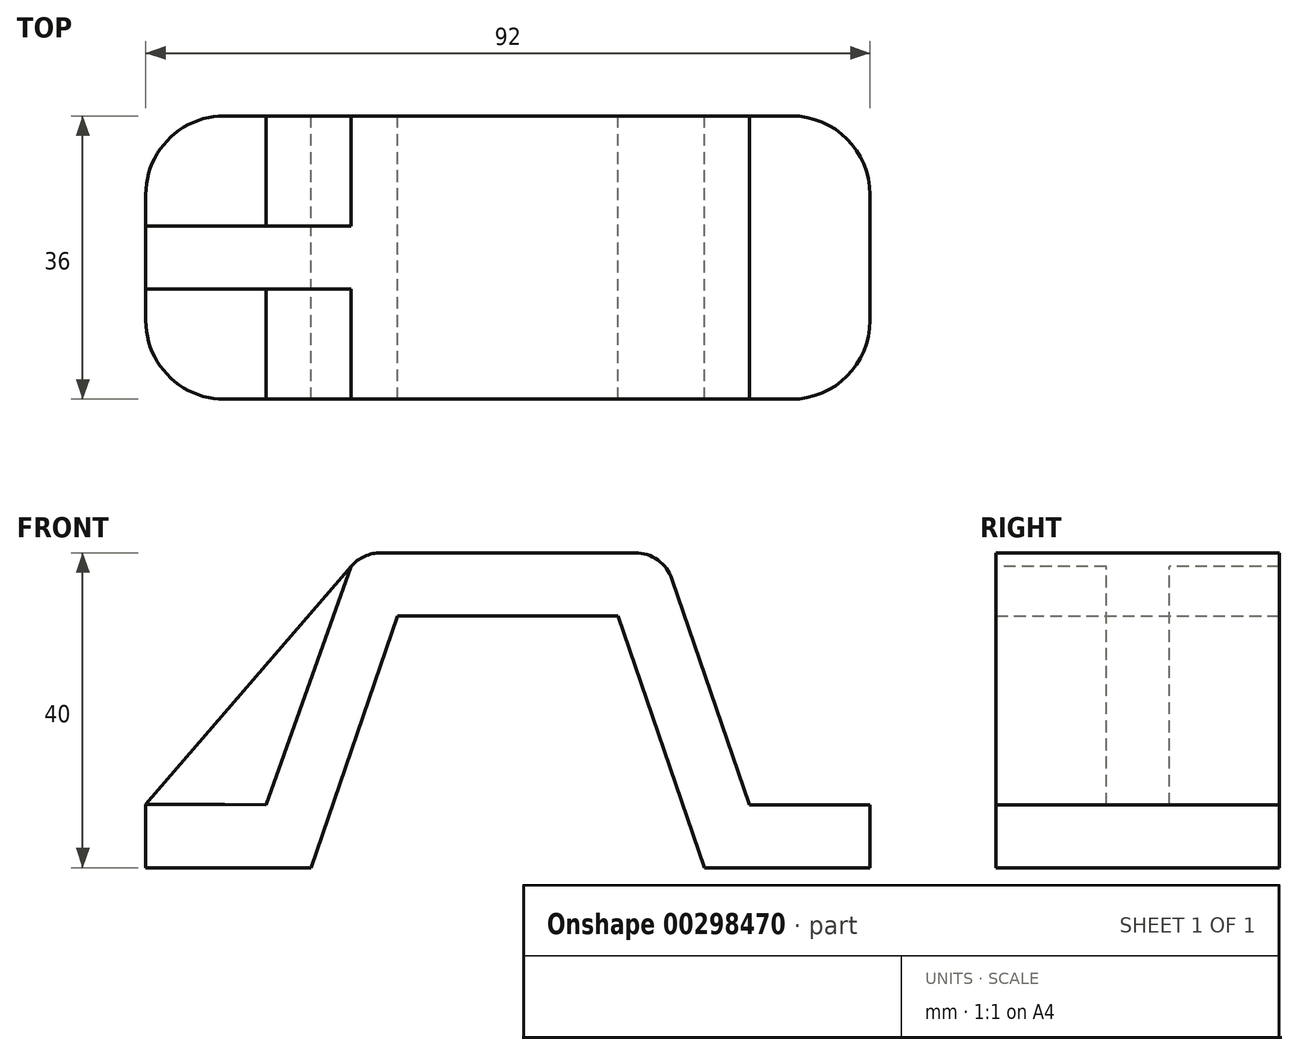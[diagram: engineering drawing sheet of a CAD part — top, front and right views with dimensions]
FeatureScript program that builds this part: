
annotation { "Feature Type Name" : "Feature", "Feature Type Description" : "" }
export const myFeature = defineFeature(function(context is Context, id is Id, definition is map)
    precondition{}
    {
        {
            var Q0;
            Q0=qCreatedBy(makeId("Front.planeOp"),FACE);
            var sketch = newSketch(context, id + "F0", { "sketchPlane" : qUnion([Q0])});
            skLineSegment(sketch, "E0", {"start": v(0, 0) * mm, "end": v(21, 0) * mm});
            skLineSegment(sketch, "E1", {"start": v(21, 0) * mm, "end": v(71, 0) * mm});
            skLineSegment(sketch, "E2", {"start": v(71, 0) * mm, "end": v(92, 0) * mm});
            skLineSegment(sketch, "E3", {"start": v(92, 0) * mm, "end": v(92, 8) * mm});
            skLineSegment(sketch, "E4", {"start": v(0, 0) * mm, "end": v(0, 8) * mm});
            skLineSegment(sketch, "E5", {"start": v(46, 0) * mm, "end": v(46, 32) * mm});
            skLineSegment(sketch, "E6", {"start": v(46, 32) * mm, "end": v(32, 32) * mm});
            skLineSegment(sketch, "E7", {"start": v(46, 32) * mm, "end": v(60, 32) * mm});
            skLineSegment(sketch, "E8", {"start": v(32, 32) * mm, "end": v(21, 0) * mm});
            skLineSegment(sketch, "E9", {"start": v(60, 32) * mm, "end": v(71, 0) * mm});
            skLineSegment(sketch, "E10", {"start": v(24.43, 34.6) * mm, "end": v(15.3, 8) * mm});
            skLineSegment(sketch, "E11", {"start": v(15.3, 8) * mm, "end": v(0, 8) * mm});
            skLineSegment(sketch, "E12", {"start": v(67.57, 34.6) * mm, "end": v(76.7, 8) * mm});
            skLineSegment(sketch, "E13", {"start": v(76.7, 8) * mm, "end": v(92, 8) * mm});
            skLineSegment(sketch, "E14", {"start": v(46, 40) * mm, "end": v(29.86, 40) * mm});
            skLineSegment(sketch, "E15", {"start": v(29.86, 40) * mm, "end": v(62.14, 40) * mm});
            skLineSegment(sketch, "E16", {"start": v(24.43, 34.6) * mm, "end": v(25.13, 36.63) * mm});
            skLineSegment(sketch, "E17", {"start": v(67.57, 34.6) * mm, "end": v(66.87, 36.63) * mm});
            skPoint(sketch, "E18.orphan", {"position": v(67.57, 40) * mm});
            skPoint(sketch, "E19.orphan", {"position": v(24.43, 40) * mm});
            skArc(sketch, "E20", {"start": v(29.86, 40) * mm, "mid": v(26.95, 39.07) * mm, "end": v(25.13, 36.63) * mm});
            skArc(sketch, "E21.MirrorC", {"start": v(62.14, 40) * mm, "mid": v(65.05, 39.07) * mm, "end": v(66.87, 36.63) * mm});
            skPoint(sketch, "E22.orphan", {"position": v(26.3, 40) * mm});
            skPoint(sketch, "E23.orphan", {"position": v(65.7, 40) * mm});
            skSolve(sketch);
        }
        {
            var Q0;
            Q0=makeQuery(id+"F0.imprint","IMPRINT",FACE,{"disambiguationData":[TD([[makeQuery(id+"F0.imprint","IMPRINT",EDGE,{"derivedFrom":sQuery(id+"F0.wireOp",EDGE,"E0")}),1.0]])]});
            extrude(context, id + "F1", {"entities" : qUnion([Q0]), "depth" : 36 * mm});
        }
        {
            var Q0;
            Q0=makeQuery(id+"F1.opExtrude","CAP_EDGE",EDGE,{"disambiguationData":[OSD([sQuery(id+"F0.wireOp",EDGE,"E3")])],"isStart":false});
            var Q1;
            Q1=makeQuery(id+"F1.opExtrude","CAP_EDGE",EDGE,{"disambiguationData":[OSD([sQuery(id+"F0.wireOp",EDGE,"E3")])],"isStart":true});
            var Q2;
            Q2=makeQuery(id+"F1.opExtrude","CAP_EDGE",EDGE,{"disambiguationData":[OSD([sQuery(id+"F0.wireOp",EDGE,"E4")])],"isStart":false});
            var Q3;
            Q3=makeQuery(id+"F1.opExtrude","CAP_EDGE",EDGE,{"disambiguationData":[OSD([sQuery(id+"F0.wireOp",EDGE,"E4")])],"isStart":true});
            fillet(context, id + "F2", {"entities" : qUnion([Q0, Q1, Q2, Q3]), "radius" : 10 * mm, "tangentPropagation" : true, "allowEdgeOverflow" : false});
        }
        {
            var Q0;
            Q0=makeQuery(id+"F1.opExtrude","CAP_FACE",FACE,{"disambiguationData":[OSD([sQuery(id+"F0.wireOp",EDGE,"E0"),sQuery(id+"F0.wireOp",EDGE,"E2"),sQuery(id+"F0.wireOp",EDGE,"E3"),sQuery(id+"F0.wireOp",EDGE,"E4"),sQuery(id+"F0.wireOp",EDGE,"E6"),sQuery(id+"F0.wireOp",EDGE,"E7"),sQuery(id+"F0.wireOp",EDGE,"E8"),sQuery(id+"F0.wireOp",EDGE,"E9"),sQuery(id+"F0.wireOp",EDGE,"E10"),sQuery(id+"F0.wireOp",EDGE,"E11"),sQuery(id+"F0.wireOp",EDGE,"E12"),sQuery(id+"F0.wireOp",EDGE,"E13"),sQuery(id+"F0.wireOp",EDGE,"E15"),sQuery(id+"F0.wireOp",EDGE,"E16"),sQuery(id+"F0.wireOp",EDGE,"E17"),sQuery(id+"F0.wireOp",EDGE,"E20"),sQuery(id+"F0.wireOp",EDGE,"E21.MirrorC")])],"isStart":false});
            var sketch = newSketch(context, id + "F3", { "sketchPlane" : qUnion([Q0])});
            skLineSegment(sketch, "E24", {"start": v(0, 8) * mm, "end": v(26.95, 39.29) * mm});
            skPoint(sketch, "E24.endSnap0", {"position": v(26.95, 39.07) * mm});
            skLineSegment(sketch, "E25", {"start": v(0, 8) * mm, "end": v(15.3, 8) * mm});
            skLineSegment(sketch, "E26", {"start": v(15.3, 8) * mm, "end": v(25.13, 36.63) * mm});
            skArc(sketch, "E27", {"start": v(25.13, 36.63) * mm, "mid": v(25.85, 38) * mm, "end": v(26.95, 39.07) * mm});
            skSolve(sketch);
        }
        {
            var Q0;
            Q0 = qSketchRegion(id + "F3", true);
            extrude(context, id + "F4", {"entities" : qUnion([Q0]), "operationType" : NewBodyOperationType.ADD, "oppositeDirection" : true, "depth" : 36 * mm});
        }
        {
            var Q0;
            Q0=makeQuery(id+"F4.boolean.opBoolean","MERGE",FACE,{"derivedFrom":[makeQuery(id+"F1.opExtrude","CAP_FACE",FACE,{"disambiguationData":[OSD([sQuery(id+"F0.wireOp",EDGE,"E0"),sQuery(id+"F0.wireOp",EDGE,"E2"),sQuery(id+"F0.wireOp",EDGE,"E3"),sQuery(id+"F0.wireOp",EDGE,"E4"),sQuery(id+"F0.wireOp",EDGE,"E6"),sQuery(id+"F0.wireOp",EDGE,"E7"),sQuery(id+"F0.wireOp",EDGE,"E8"),sQuery(id+"F0.wireOp",EDGE,"E9"),sQuery(id+"F0.wireOp",EDGE,"E10"),sQuery(id+"F0.wireOp",EDGE,"E11"),sQuery(id+"F0.wireOp",EDGE,"E12"),sQuery(id+"F0.wireOp",EDGE,"E13"),sQuery(id+"F0.wireOp",EDGE,"E15"),sQuery(id+"F0.wireOp",EDGE,"E16"),sQuery(id+"F0.wireOp",EDGE,"E17"),sQuery(id+"F0.wireOp",EDGE,"E20"),sQuery(id+"F0.wireOp",EDGE,"E21.MirrorC")])],"isStart":false}),makeQuery(id+"F4.opExtrude","CAP_FACE",FACE,{"disambiguationData":[OSD([sQuery(id+"F3.wireOp",EDGE,"E24"),sQuery(id+"F3.wireOp",EDGE,"E25"),sQuery(id+"F3.wireOp",EDGE,"E26"),sQuery(id+"F3.wireOp",EDGE,"E27")])],"isStart":true})]});
            var sketch = newSketch(context, id + "F5", { "sketchPlane" : qUnion([Q0])});
            skLineSegment(sketch, "E28", {"start": v(15.3, 8) * mm, "end": v(26.07, 38.26) * mm});
            skLineSegment(sketch, "E29", {"start": v(26.07, 38.26) * mm, "end": v(0, 8) * mm});
            skLineSegment(sketch, "E30", {"start": v(0, 8) * mm, "end": v(15.3, 8) * mm});
            skSolve(sketch);
        }
        {
            var Q0;
            Q0 = qSketchRegion(id + "F5", true);
            extrude(context, id + "F6", {"entities" : qUnion([Q0]), "operationType" : NewBodyOperationType.REMOVE, "oppositeDirection" : true, "depth" : 14 * mm});
        }
        {
            var Q0;
            Q0=makeQuery(id+"F4.boolean.opBoolean","MERGE",FACE,{"derivedFrom":[makeQuery(id+"F1.opExtrude","CAP_FACE",FACE,{"disambiguationData":[OSD([sQuery(id+"F0.wireOp",EDGE,"E0"),sQuery(id+"F0.wireOp",EDGE,"E2"),sQuery(id+"F0.wireOp",EDGE,"E3"),sQuery(id+"F0.wireOp",EDGE,"E4"),sQuery(id+"F0.wireOp",EDGE,"E6"),sQuery(id+"F0.wireOp",EDGE,"E7"),sQuery(id+"F0.wireOp",EDGE,"E8"),sQuery(id+"F0.wireOp",EDGE,"E9"),sQuery(id+"F0.wireOp",EDGE,"E10"),sQuery(id+"F0.wireOp",EDGE,"E11"),sQuery(id+"F0.wireOp",EDGE,"E12"),sQuery(id+"F0.wireOp",EDGE,"E13"),sQuery(id+"F0.wireOp",EDGE,"E15"),sQuery(id+"F0.wireOp",EDGE,"E16"),sQuery(id+"F0.wireOp",EDGE,"E17"),sQuery(id+"F0.wireOp",EDGE,"E20"),sQuery(id+"F0.wireOp",EDGE,"E21.MirrorC")])],"isStart":true}),makeQuery(id+"F4.opExtrude","CAP_FACE",FACE,{"disambiguationData":[OSD([sQuery(id+"F3.wireOp",EDGE,"E24"),sQuery(id+"F3.wireOp",EDGE,"E25"),sQuery(id+"F3.wireOp",EDGE,"E26"),sQuery(id+"F3.wireOp",EDGE,"E27")])],"isStart":false})]});
            var sketch = newSketch(context, id + "F7", { "sketchPlane" : qUnion([Q0])});
            skLineSegment(sketch, "E31", {"start": v(-15.3, 8) * mm, "end": v(-26.07, 38.26) * mm});
            skLineSegment(sketch, "E32", {"start": v(-26.07, 38.26) * mm, "end": v(0, 8) * mm});
            skLineSegment(sketch, "E33", {"start": v(0, 8) * mm, "end": v(-15.3, 8) * mm});
            skSolve(sketch);
        }
        {
            var Q0;
            Q0 = qSketchRegion(id + "F7", true);
            extrude(context, id + "F8", {"entities" : qUnion([Q0]), "operationType" : NewBodyOperationType.REMOVE, "oppositeDirection" : true, "depth" : 14 * mm});
        }
    });
